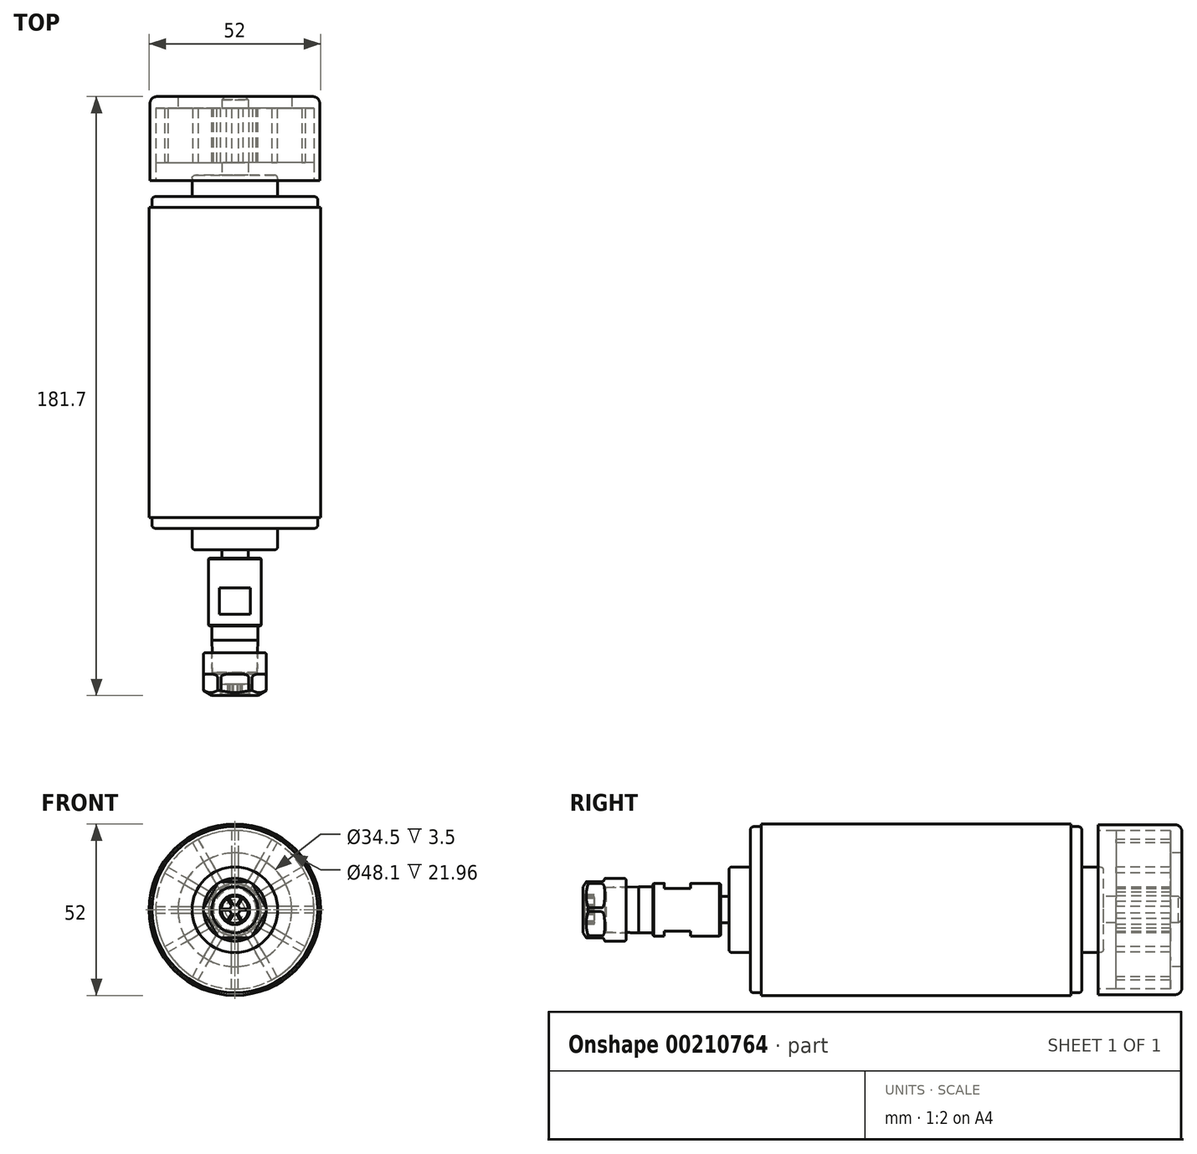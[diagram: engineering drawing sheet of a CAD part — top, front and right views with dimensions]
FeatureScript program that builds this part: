
annotation { "Feature Type Name" : "Feature", "Feature Type Description" : "" }
export const myFeature = defineFeature(function(context is Context, id is Id, definition is map)
    precondition{}
    {
        {
            var Q0;
            Q0=qCreatedBy(makeId("Right.planeOp"),FACE);
            var sketch = newSketch(context, id + "F0", { "sketchPlane" : qUnion([Q0])});
            skLineSegment(sketch, "E0", {"start": v(-129, 0) * mm, "end": v(123.78, 0) * mm, "construction": true});
            skLineSegment(sketch, "E1", {"start": v(-68.75, 0) * mm, "end": v(68.75, 0) * mm});
            skLineSegment(sketch, "E2", {"start": v(68.75, 0) * mm, "end": v(68.75, 25.75) * mm, "construction": true});
            skLineSegment(sketch, "E3", {"start": v(68.75, 25.75) * mm, "end": v(43.3, 25.75) * mm});
            skLineSegment(sketch, "E4", {"start": v(43.3, 25.75) * mm, "end": v(43.3, 24.05) * mm});
            skLineSegment(sketch, "E5", {"start": v(43.3, 24.05) * mm, "end": v(48.75, 24.05) * mm});
            skLineSegment(sketch, "E6", {"start": v(48.75, 24.05) * mm, "end": v(48.75, 4) * mm});
            skLineSegment(sketch, "E7", {"start": v(48.75, 4) * mm, "end": v(44.93, 4) * mm});
            skLineSegment(sketch, "E8", {"start": v(44.93, 4) * mm, "end": v(44.93, 13) * mm});
            skLineSegment(sketch, "E9", {"start": v(44.93, 13) * mm, "end": v(38.39, 13) * mm});
            skLineSegment(sketch, "E10", {"start": v(38.39, 13) * mm, "end": v(38.39, 25.2) * mm});
            skLineSegment(sketch, "E11", {"start": v(38.39, 25.2) * mm, "end": v(35.09, 25.2) * mm});
            skLineSegment(sketch, "E12", {"start": v(35.09, 25.2) * mm, "end": v(35.09, 26) * mm});
            skLineSegment(sketch, "E13", {"start": v(35.09, 26) * mm, "end": v(-58.91, 26) * mm});
            skLineSegment(sketch, "E14", {"start": v(-58.91, 26) * mm, "end": v(-58.91, 25.2) * mm});
            skLineSegment(sketch, "E15", {"start": v(-58.91, 25.2) * mm, "end": v(-62.21, 25.2) * mm});
            skLineSegment(sketch, "E16", {"start": v(-62.2, 25.2) * mm, "end": v(-62.2, 13) * mm});
            skLineSegment(sketch, "E17", {"start": v(-62.21, 13) * mm, "end": v(-68.75, 13) * mm});
            skLineSegment(sketch, "E18", {"start": v(-68.75, 13) * mm, "end": v(-68.75, 0) * mm});
            skLineSegment(sketch, "E19", {"start": v(68.75, 0) * mm, "end": v(68.75, 4) * mm});
            skLineSegment(sketch, "E20", {"start": v(68.75, 4) * mm, "end": v(65.25, 4) * mm});
            skLineSegment(sketch, "E21", {"start": v(65.25, 4) * mm, "end": v(65.25, 17.25) * mm});
            skLineSegment(sketch, "E22", {"start": v(65.25, 17.25) * mm, "end": v(68.75, 17.25) * mm});
            skLineSegment(sketch, "E23", {"start": v(68.75, 25.75) * mm, "end": v(68.75, 17.25) * mm});
            skLineSegment(sketch, "E24", {"start": v(-71.25, 4) * mm, "end": v(-68.75, 4) * mm});
            skLineSegment(sketch, "E25", {"start": v(-106.25, 0) * mm, "end": v(-106.25, 6.75) * mm});
            skLineSegment(sketch, "E26", {"start": v(-106.25, 6.75) * mm, "end": v(-96.15, 7) * mm});
            skLineSegment(sketch, "E27", {"start": v(-96.15, 7) * mm, "end": v(-91.85, 7) * mm});
            skLineSegment(sketch, "E28", {"start": v(-91.85, 7) * mm, "end": v(-91.85, 8) * mm});
            skLineSegment(sketch, "E29", {"start": v(-91.85, 8) * mm, "end": v(-71.25, 8) * mm});
            skLineSegment(sketch, "E30", {"start": v(-68.75, 0) * mm, "end": v(-106.25, 0) * mm});
            skLineSegment(sketch, "E31", {"start": v(-71.25, 8) * mm, "end": v(-71.25, 0) * mm});
            skSolve(sketch);
        }
        {
            var Q0;
            Q0=makeQuery(id+"F0.imprint","IMPRINT",FACE,{"disambiguationData":[TD([[makeQuery(id+"F0.imprint","IMPRINT",EDGE,{"derivedFrom":sQuery(id+"F0.wireOp",EDGE,"E1")}),1.0]])]});
            var Q1;
            {var subQ3=sQuery(id+"F0.wireOp",EDGE,"E24");Q1=makeQuery(id+"F0.imprint","IMPRINT",FACE,{"disambiguationData":[TD([[makeQuery(id+"F0.imprint","IMPRINT",EDGE,{"derivedFrom":subQ3}),-1.0]])]});}
            var Q2;
            {var subQ0=sQuery(id+"F0.wireOp",EDGE,"E25");Q2=makeQuery(id+"F0.imprint","IMPRINT",FACE,{"disambiguationData":[TD([[makeQuery(id+"F0.imprint","IMPRINT",EDGE,{"derivedFrom":subQ0}),-1.0]])]});}
            var Q3;
            Q3=sQuery(id+"F0.wireOp",EDGE,"E0");
            revolve(context, id + "F1", {"entities" : qUnion([Q0, Q1, Q2]), "axis" : qUnion([Q3]), "revolveType" : RevolveType.FULL});
        }
        {
            var Q0;
            Q0=makeQuery(id+"F1.opRevolve","SWEPT_EDGE",EDGE,{"disambiguationData":[OSD([sQuery(id+"F0.wireOp",EDGE,"E3"),sQuery(id+"F0.wireOp",EDGE,"E23")])]});
            fillet(context, id + "F2", {"entities" : qUnion([Q0]), "radius" : 2 * mm, "tangentPropagation" : true, "allowEdgeOverflow" : false});
        }
        {
            var Q0;
            Q0=makeQuery(id+"F1.opRevolve","SWEPT_EDGE",EDGE,{"disambiguationData":[OSD([sQuery(id+"F0.wireOp",EDGE,"E10"),sQuery(id+"F0.wireOp",EDGE,"E11")])]});
            var Q1;
            Q1=makeQuery(id+"F1.opRevolve","SWEPT_EDGE",EDGE,{"disambiguationData":[OSD([sQuery(id+"F0.wireOp",EDGE,"E15"),sQuery(id+"F0.wireOp",EDGE,"E16")])]});
            var Q2;
            Q2=makeQuery(id+"F1.opRevolve","SWEPT_EDGE",EDGE,{"disambiguationData":[OSD([sQuery(id+"F0.wireOp",EDGE,"E17"),sQuery(id+"F0.wireOp",EDGE,"E18")])]});
            var Q3;
            Q3=makeQuery(id+"F1.opRevolve","SWEPT_EDGE",EDGE,{"disambiguationData":[OSD([sQuery(id+"F0.wireOp",EDGE,"E8"),sQuery(id+"F0.wireOp",EDGE,"E9")])]});
            fillet(context, id + "F3", {"entities" : qUnion([Q0, Q1, Q2, Q3]), "radius" : 1 * mm, "tangentPropagation" : true, "allowEdgeOverflow" : false});
        }
        {
            var Q0;
            Q0=makeQuery(id+"F1.opRevolve","SWEPT_EDGE",EDGE,{"disambiguationData":[OSD([sQuery(id+"F0.wireOp",EDGE,"E19"),sQuery(id+"F0.wireOp",EDGE,"E20")])]});
            chamfer(context, id + "F4", {"entities" : qUnion([Q0]), "width" : 1 * mm, "tangentPropagation" : true});
        }
        {
            var Q0;
            Q0=makeQuery(id+"F1.opRevolve","SWEPT_EDGE",EDGE,{"disambiguationData":[OSD([sQuery(id+"F0.wireOp",EDGE,"E29"),sQuery(id+"F0.wireOp",EDGE,"E31")])]});
            var Q1;
            Q1=makeQuery(id+"F1.opRevolve","SWEPT_EDGE",EDGE,{"disambiguationData":[OSD([sQuery(id+"F0.wireOp",EDGE,"E28"),sQuery(id+"F0.wireOp",EDGE,"E29")])]});
            var Q2;
            Q2=makeQuery(id+"F1.opRevolve","SWEPT_EDGE",EDGE,{"disambiguationData":[OSD([sQuery(id+"F0.wireOp",EDGE,"E25"),sQuery(id+"F0.wireOp",EDGE,"E26")])]});
            chamfer(context, id + "F5", {"entities" : qUnion([Q0, Q1, Q2]), "width" : .3 * mm, "tangentPropagation" : true});
        }
        {
            var Q0;
            Q0=qCreatedBy(makeId("Right.planeOp"),FACE);
            var sketch = newSketch(context, id + "F6", { "sketchPlane" : qUnion([Q0])});
            skLineSegment(sketch, "E32.bottom", {"start": v(-88.35, 9) * mm, "end": v(-80.35, 9) * mm});
            skLineSegment(sketch, "E32.top", {"start": v(-88.35, 6.5) * mm, "end": v(-80.35, 6.5) * mm});
            skLineSegment(sketch, "E32.left", {"start": v(-88.35, 9) * mm, "end": v(-88.35, 6.5) * mm});
            skLineSegment(sketch, "E32.right", {"start": v(-80.35, 9) * mm, "end": v(-80.35, 6.5) * mm});
            skLineSegment(sketch, "E33", {"start": v(-60.08, 0) * mm, "end": v(-87.32, 0) * mm, "construction": true});
            skLineSegment(sketch, "E34.MirrorCS", {"start": v(-80.35, -9) * mm, "end": v(-80.35, -6.5) * mm});
            skLineSegment(sketch, "E35.MirrorCS", {"start": v(-88.35, -9) * mm, "end": v(-88.35, -6.5) * mm});
            skLineSegment(sketch, "E36.MirrorCS", {"start": v(-88.35, -9) * mm, "end": v(-80.35, -9) * mm});
            skLineSegment(sketch, "E37.MirrorCS", {"start": v(-88.35, -6.5) * mm, "end": v(-80.35, -6.5) * mm});
            skSolve(sketch);
        }
        {
            var Q0;
            Q0 = qSketchRegion(id + "F6", true);
            extrude(context, id + "F7", {"entities" : qUnion([Q0]), "operationType" : NewBodyOperationType.REMOVE, "endBound" : BoundingType.SYMMETRIC, "depth" : 25 * mm});
        }
        {
            var Q0;
            Q0=qCreatedBy(makeId("Right.planeOp"),FACE);
            var sketch = newSketch(context, id + "F8", { "sketchPlane" : qUnion([Q0])});
            skLineSegment(sketch, "E38", {"start": v(0, 0) * mm, "end": v(-99.95, 0) * mm, "construction": true});
            skLineSegment(sketch, "E39", {"start": v(-99.95, 0) * mm, "end": v(-112.95, 0) * mm});
            skLineSegment(sketch, "E40", {"start": v(-112.95, 0) * mm, "end": v(-112.95, 9.5) * mm});
            skLineSegment(sketch, "E41", {"start": v(-112.95, 9.5) * mm, "end": v(-99.95, 9.5) * mm});
            skLineSegment(sketch, "E42", {"start": v(-99.95, 9.5) * mm, "end": v(-99.95, 0) * mm});
            skLineSegment(sketch, "E43", {"start": v(-106.42, 0) * mm, "end": v(-106.42, 6.84) * mm});
            skLineSegment(sketch, "E44", {"start": v(-106.42, 6.84) * mm, "end": v(-99.95, 7.03) * mm});
            skSolve(sketch);
        }
        {
            var Q0;
            {var subQ3=sQuery(id+"F8.wireOp",EDGE,"E40");Q0=makeQuery(id+"F8.imprint","IMPRINT",FACE,{"disambiguationData":[TD([[makeQuery(id+"F8.imprint","IMPRINT",EDGE,{"derivedFrom":subQ3}),-1.0]])]});}
            var Q1;
            Q1=sQuery(id+"F8.wireOp",EDGE,"E38");
            revolve(context, id + "F9", {"entities" : qUnion([Q0]), "axis" : qUnion([Q1]), "revolveType" : RevolveType.FULL});
        }
        {
            var Q0;
            Q0=makeQuery(id+"F9.opRevolve","SWEPT_EDGE",EDGE,{"disambiguationData":[OSD([sQuery(id+"F8.wireOp",EDGE,"E41"),sQuery(id+"F8.wireOp",EDGE,"E42")])]});
            fillet(context, id + "F10", {"entities" : qUnion([Q0]), "radius" : .5 * mm, "tangentPropagation" : true, "allowEdgeOverflow" : false});
        }
        {
            var Q0;
            Q0=qCreatedBy(makeId("Right.planeOp"),FACE);
            var sketch = newSketch(context, id + "F11", { "sketchPlane" : qUnion([Q0])});
            skLineSegment(sketch, "E45", {"start": v(-112.95, 7) * mm, "end": v(-111.45, 9.5) * mm});
            skLineSegment(sketch, "E46", {"start": v(-111.45, 9.5) * mm, "end": v(-112.95, 9.5) * mm});
            skLineSegment(sketch, "E47", {"start": v(-112.95, 9.5) * mm, "end": v(-112.95, 7) * mm});
            skLineSegment(sketch, "E48", {"start": v(0, 0) * mm, "end": v(-3.44, 0) * mm});
            skLineSegment(sketch, "E49", {"start": v(-3.44, 0) * mm, "end": v(-117.43, 0) * mm, "construction": true});
            skSolve(sketch);
        }
        {
            var Q0;
            Q0 = qSketchRegion(id + "F11", true);
            var Q1;
            Q1=sQuery(id+"F11.wireOp",EDGE,"E49");
            revolve(context, id + "F12", {"operationType" : NewBodyOperationType.REMOVE, "entities" : qUnion([Q0]), "axis" : qUnion([Q1]), "revolveType" : RevolveType.FULL, "oppositeDirection" : true});
        }
        {
            var Q0;
            Q0=makeQuery(id+"F9.opRevolve","SWEPT_FACE",FACE,{"disambiguationData":[OSD([sQuery(id+"F8.wireOp",EDGE,"E40")])]});
            var sketch = newSketch(context, id + "F13", { "sketchPlane" : qUnion([Q0])});
            skCircle(sketch, "E50.cCircle", {"center": v(0, 0) * mm, "radius": 8.5 * mm, "construction": true});
            skLineSegment(sketch, "E50.0", {"start": v(-4.9, 8.5) * mm, "end": v(4.9, 8.5) * mm});
            skLineSegment(sketch, "E50.1", {"start": v(4.9, 8.5) * mm, "end": v(9.81, 0) * mm});
            skLineSegment(sketch, "E50.2", {"start": v(9.81, 0) * mm, "end": v(4.9, -8.5) * mm});
            skLineSegment(sketch, "E50.3", {"start": v(4.9, -8.5) * mm, "end": v(-4.9, -8.5) * mm});
            skLineSegment(sketch, "E50.4", {"start": v(-4.9, -8.5) * mm, "end": v(-9.81, 0) * mm});
            skLineSegment(sketch, "E50.5", {"start": v(-9.81, 0) * mm, "end": v(-4.9, 8.5) * mm});
            skPoint(sketch, "E50.0.midPoint", {"position": v(0, 8.5) * mm});
            skCircle(sketch, "E51", {"center": v(0, 0) * mm, "radius": 12 * mm});
            skLineSegment(sketch, "E52", {"start": v(0, 8.5) * mm, "end": v(0, 9.5) * mm, "construction": true});
            skSolve(sketch);
        }
        {
            var Q0;
            Q0=makeQuery(id+"F13.imprint","IMPRINT",FACE,{"disambiguationData":[TD([[makeQuery(id+"F13.imprint","IMPRINT",EDGE,{"derivedFrom":sQuery(id+"F13.wireOp",EDGE,"E50.0")}),1.0]])]});
            extrude(context, id + "F14", {"entities" : qUnion([Q0]), "operationType" : NewBodyOperationType.REMOVE, "oppositeDirection" : true, "depth" : 6.5 * mm});
        }
        {
            var Q0;
            Q0=makeQuery(id+"F14.boolean.opBoolean","COPY",EDGE,{"derivedFrom":makeQuery(id+"F14.opExtrude","CAP_EDGE",EDGE,{"disambiguationData":[OSD([sQuery(id+"F13.wireOp",EDGE,"E50.0")])],"isStart":false})});
            var Q1;
            Q1=makeQuery(id+"F14.boolean.opBoolean","COPY",EDGE,{"derivedFrom":makeQuery(id+"F14.opExtrude","CAP_EDGE",EDGE,{"disambiguationData":[OSD([sQuery(id+"F13.wireOp",EDGE,"E50.1")])],"isStart":false})});
            var Q2;
            Q2=makeQuery(id+"F14.boolean.opBoolean","COPY",EDGE,{"derivedFrom":makeQuery(id+"F14.opExtrude","CAP_EDGE",EDGE,{"disambiguationData":[OSD([sQuery(id+"F13.wireOp",EDGE,"E50.2")])],"isStart":false})});
            var Q3;
            Q3=makeQuery(id+"F14.boolean.opBoolean","COPY",EDGE,{"derivedFrom":makeQuery(id+"F14.opExtrude","CAP_EDGE",EDGE,{"disambiguationData":[OSD([sQuery(id+"F13.wireOp",EDGE,"E50.3")])],"isStart":false})});
            var Q4;
            Q4=makeQuery(id+"F14.boolean.opBoolean","COPY",EDGE,{"derivedFrom":makeQuery(id+"F14.opExtrude","CAP_EDGE",EDGE,{"disambiguationData":[OSD([sQuery(id+"F13.wireOp",EDGE,"E50.4")])],"isStart":false})});
            var Q5;
            Q5=makeQuery(id+"F14.boolean.opBoolean","COPY",EDGE,{"derivedFrom":makeQuery(id+"F14.opExtrude","CAP_EDGE",EDGE,{"disambiguationData":[OSD([sQuery(id+"F13.wireOp",EDGE,"E50.5")])],"isStart":false})});
            fillet(context, id + "F15", {"entities" : qUnion([Q0, Q1, Q2, Q3, Q4, Q5]), "radius" : 1 * mm, "tangentPropagation" : true, "allowEdgeOverflow" : false});
        }
        {
            var Q0;
            Q0=makeQuery(id+"F9.opRevolve","SWEPT_FACE",FACE,{"disambiguationData":[OSD([sQuery(id+"F8.wireOp",EDGE,"E40")])]});
            var sketch = newSketch(context, id + "F16", { "sketchPlane" : qUnion([Q0])});
            skCircle(sketch, "E53", {"center": v(0, 0) * mm, "radius": 4.5 * mm});
            skSolve(sketch);
        }
        {
            var Q0;
            Q0 = qSketchRegion(id + "F16", true);
            extrude(context, id + "F17", {"entities" : qUnion([Q0]), "operationType" : NewBodyOperationType.REMOVE, "oppositeDirection" : true, "depth" : .4 * mm});
        }
        {
            var Q0;
            Q0=makeQuery(id+"F17.boolean.opBoolean","COPY",FACE,{"derivedFrom":makeQuery(id+"F17.opExtrude","CAP_FACE",FACE,{"disambiguationData":[OSD([sQuery(id+"F16.wireOp",EDGE,"E53")])],"isStart":false})});
            var sketch = newSketch(context, id + "F18", { "sketchPlane" : qUnion([Q0])});
            skCircle(sketch, "E54", {"center": v(0, 0) * mm, "radius": 4.5 * mm});
            skArc(sketch, "E55", {"start": v(-0.92, 1.19) * mm, "mid": v(-1.3, 0.75) * mm, "end": v(-1.49, 0.2) * mm});
            skLineSegment(sketch, "E56", {"start": v(0, 4.5) * mm, "end": v(0, 0) * mm, "construction": true});
            skLineSegment(sketch, "E57", {"start": v(-2.25, 3.9) * mm, "end": v(0, 0) * mm, "construction": true});
            skLineSegment(sketch, "E58", {"start": v(-2.22, 3.45) * mm, "end": v(-0.92, 1.19) * mm});
            skLineSegment(sketch, "E59", {"start": v(-1.87, 3.65) * mm, "end": v(-0.57, 1.39) * mm});
            skArc(sketch, "E60", {"start": v(-2.22, 3.45) * mm, "mid": v(-3.55, 2.05) * mm, "end": v(-4.1, 0.2) * mm});
            skLineSegment(sketch, "E61.1.0", {"start": v(-4.1, 0.2) * mm, "end": v(-1.49, 0.2) * mm});
            skLineSegment(sketch, "E61.1.1", {"start": v(-4.1, -0.2) * mm, "end": v(-1.49, -0.2) * mm});
            skLineSegment(sketch, "E61.2.0", {"start": v(-2.22, -3.45) * mm, "end": v(-0.92, -1.19) * mm});
            skLineSegment(sketch, "E61.2.1", {"start": v(-1.87, -3.65) * mm, "end": v(-0.57, -1.39) * mm});
            skLineSegment(sketch, "E61.3.0", {"start": v(1.87, -3.65) * mm, "end": v(0.57, -1.39) * mm});
            skLineSegment(sketch, "E61.3.1", {"start": v(2.22, -3.45) * mm, "end": v(0.92, -1.19) * mm});
            skLineSegment(sketch, "E61.4.0", {"start": v(4.1, -0.2) * mm, "end": v(1.49, -0.2) * mm});
            skLineSegment(sketch, "E61.4.1", {"start": v(4.1, 0.2) * mm, "end": v(1.49, 0.2) * mm});
            skLineSegment(sketch, "E61.5.0", {"start": v(2.22, 3.45) * mm, "end": v(0.92, 1.19) * mm});
            skLineSegment(sketch, "E61.5.1", {"start": v(1.87, 3.65) * mm, "end": v(0.57, 1.39) * mm});
            skArc(sketch, "E62.trimOffspring", {"start": v(0.57, 1.39) * mm, "mid": v(0, 1.5) * mm, "end": v(-0.57, 1.39) * mm});
            skArc(sketch, "E63.trimOffspring", {"start": v(1.87, 3.65) * mm, "mid": v(0, 4.1) * mm, "end": v(-1.87, 3.65) * mm});
            skArc(sketch, "E64.trimOffspring", {"start": v(4.1, 0.2) * mm, "mid": v(3.55, 2.05) * mm, "end": v(2.22, 3.45) * mm});
            skArc(sketch, "E65.trimOffspring", {"start": v(1.49, 0.2) * mm, "mid": v(1.3, 0.75) * mm, "end": v(0.92, 1.19) * mm});
            skArc(sketch, "E66.trimOffspring", {"start": v(0.92, -1.19) * mm, "mid": v(1.3, -0.75) * mm, "end": v(1.49, -0.2) * mm});
            skArc(sketch, "E67.trimOffspring", {"start": v(2.22, -3.45) * mm, "mid": v(3.55, -2.05) * mm, "end": v(4.1, -0.2) * mm});
            skArc(sketch, "E68.trimOffspring", {"start": v(-1.87, -3.65) * mm, "mid": v(0, -4.1) * mm, "end": v(1.87, -3.65) * mm});
            skArc(sketch, "E69.trimOffspring", {"start": v(-0.57, -1.39) * mm, "mid": v(0, -1.5) * mm, "end": v(0.57, -1.39) * mm});
            skArc(sketch, "E70.trimOffspring", {"start": v(-1.49, -0.2) * mm, "mid": v(-1.3, -0.75) * mm, "end": v(-0.92, -1.19) * mm});
            skArc(sketch, "E71.trimOffspring", {"start": v(-4.1, -0.2) * mm, "mid": v(-3.55, -2.05) * mm, "end": v(-2.22, -3.45) * mm});
            skSolve(sketch);
        }
        {
            var Q0;
            Q0=makeQuery(id+"F18.imprint","IMPRINT",FACE,{"disambiguationData":[TD([[makeQuery(id+"F18.imprint","IMPRINT",EDGE,{"derivedFrom":sQuery(id+"F18.wireOp",EDGE,"E54")}),1.0]])]});
            extrude(context, id + "F19", {"entities" : qUnion([Q0]), "operationType" : NewBodyOperationType.REMOVE, "oppositeDirection" : true, "depth" : 3 * mm});
        }
        {
            var Q0;
            Q0=makeQuery(id+"F1.opRevolve","SWEPT_FACE",FACE,{"disambiguationData":[OSD([sQuery(id+"F0.wireOp",EDGE,"E21")])]});
            var sketch = newSketch(context, id + "F20", { "sketchPlane" : qUnion([Q0])});
            skArc(sketch, "E72", {"start": v(-4.33, 5.5) * mm, "mid": v(-4.95, 4.95) * mm, "end": v(-5.5, 4.33) * mm});
            skArc(sketch, "E73", {"start": v(-1, 17.22) * mm, "mid": v(-4.46, 16.66) * mm, "end": v(-7.74, 15.41) * mm});
            skLineSegment(sketch, "E74", {"start": v(0, 0) * mm, "end": v(0, 17.25) * mm, "construction": true});
            skLineSegment(sketch, "E75", {"start": v(0, 0) * mm, "end": v(4.46, 16.66) * mm, "construction": true});
            skLineSegment(sketch, "E76", {"start": v(-1, 17.22) * mm, "end": v(-1, 6.93) * mm});
            skLineSegment(sketch, "E77", {"start": v(1, 17.22) * mm, "end": v(1, 6.93) * mm});
            skLineSegment(sketch, "E78.1.0", {"start": v(-7.74, 15.41) * mm, "end": v(-2.6, 6.5) * mm});
            skLineSegment(sketch, "E78.1.1", {"start": v(-9.48, 14.41) * mm, "end": v(-4.33, 5.5) * mm});
            skLineSegment(sketch, "E78.2.0", {"start": v(-14.41, 9.48) * mm, "end": v(-5.5, 4.33) * mm});
            skLineSegment(sketch, "E78.2.1", {"start": v(-15.41, 7.74) * mm, "end": v(-6.5, 2.6) * mm});
            skLineSegment(sketch, "E78.3.0", {"start": v(-17.22, 1) * mm, "end": v(-6.93, 1) * mm});
            skLineSegment(sketch, "E78.3.1", {"start": v(-17.22, -1) * mm, "end": v(-6.93, -1) * mm});
            skLineSegment(sketch, "E78.4.0", {"start": v(-15.41, -7.74) * mm, "end": v(-6.5, -2.6) * mm});
            skLineSegment(sketch, "E78.4.1", {"start": v(-14.41, -9.48) * mm, "end": v(-5.5, -4.33) * mm});
            skLineSegment(sketch, "E78.5.0", {"start": v(-9.48, -14.41) * mm, "end": v(-4.33, -5.5) * mm});
            skLineSegment(sketch, "E78.5.1", {"start": v(-7.74, -15.41) * mm, "end": v(-2.6, -6.5) * mm});
            skLineSegment(sketch, "E78.6.0", {"start": v(-1, -17.22) * mm, "end": v(-1, -6.93) * mm});
            skLineSegment(sketch, "E78.6.1", {"start": v(1, -17.22) * mm, "end": v(1, -6.93) * mm});
            skLineSegment(sketch, "E78.7.0", {"start": v(7.74, -15.41) * mm, "end": v(2.6, -6.5) * mm});
            skLineSegment(sketch, "E78.7.1", {"start": v(9.48, -14.41) * mm, "end": v(4.33, -5.5) * mm});
            skLineSegment(sketch, "E78.8.0", {"start": v(14.41, -9.48) * mm, "end": v(5.5, -4.33) * mm});
            skLineSegment(sketch, "E78.8.1", {"start": v(15.41, -7.74) * mm, "end": v(6.5, -2.6) * mm});
            skLineSegment(sketch, "E78.9.0", {"start": v(17.22, -1) * mm, "end": v(6.93, -1) * mm});
            skLineSegment(sketch, "E78.9.1", {"start": v(17.22, 1) * mm, "end": v(6.93, 1) * mm});
            skLineSegment(sketch, "E78.10.0", {"start": v(15.41, 7.74) * mm, "end": v(6.5, 2.6) * mm});
            skLineSegment(sketch, "E78.10.1", {"start": v(14.41, 9.48) * mm, "end": v(5.5, 4.33) * mm});
            skLineSegment(sketch, "E78.11.0", {"start": v(9.48, 14.41) * mm, "end": v(4.33, 5.5) * mm});
            skLineSegment(sketch, "E78.11.1", {"start": v(7.74, 15.41) * mm, "end": v(2.6, 6.5) * mm});
            skArc(sketch, "E79.trimOffspring", {"start": v(7.74, 15.41) * mm, "mid": v(4.46, 16.66) * mm, "end": v(1, 17.22) * mm});
            skArc(sketch, "E80.trimOffspring", {"start": v(14.41, 9.48) * mm, "mid": v(12.2, 12.2) * mm, "end": v(9.48, 14.41) * mm});
            skArc(sketch, "E81.trimOffspring", {"start": v(17.22, 1) * mm, "mid": v(16.66, 4.46) * mm, "end": v(15.41, 7.74) * mm});
            skArc(sketch, "E82.trimOffspring", {"start": v(15.41, -7.74) * mm, "mid": v(16.66, -4.46) * mm, "end": v(17.22, -1) * mm});
            skArc(sketch, "E83.trimOffspring", {"start": v(9.48, -14.41) * mm, "mid": v(12.2, -12.2) * mm, "end": v(14.41, -9.48) * mm});
            skArc(sketch, "E84.trimOffspring", {"start": v(1, -17.22) * mm, "mid": v(4.46, -16.66) * mm, "end": v(7.74, -15.41) * mm});
            skArc(sketch, "E85.trimOffspring", {"start": v(-7.74, -15.41) * mm, "mid": v(-4.46, -16.66) * mm, "end": v(-1, -17.22) * mm});
            skArc(sketch, "E86.trimOffspring", {"start": v(-14.41, -9.48) * mm, "mid": v(-12.2, -12.2) * mm, "end": v(-9.48, -14.41) * mm});
            skArc(sketch, "E87.trimOffspring", {"start": v(-17.22, -1) * mm, "mid": v(-16.66, -4.46) * mm, "end": v(-15.41, -7.74) * mm});
            skArc(sketch, "E88.trimOffspring", {"start": v(-15.41, 7.74) * mm, "mid": v(-16.66, 4.46) * mm, "end": v(-17.22, 1) * mm});
            skArc(sketch, "E89.trimOffspring", {"start": v(-9.48, 14.41) * mm, "mid": v(-12.2, 12.2) * mm, "end": v(-14.41, 9.48) * mm});
            skArc(sketch, "E90.trimOffspring", {"start": v(-1, 6.93) * mm, "mid": v(-1.81, 6.76) * mm, "end": v(-2.6, 6.5) * mm});
            skArc(sketch, "E91.trimOffspring", {"start": v(2.6, 6.5) * mm, "mid": v(1.81, 6.76) * mm, "end": v(1, 6.93) * mm});
            skArc(sketch, "E92.trimOffspring", {"start": v(6.93, 1) * mm, "mid": v(6.76, 1.81) * mm, "end": v(6.5, 2.6) * mm});
            skArc(sketch, "E93.trimOffspring", {"start": v(6.5, -2.6) * mm, "mid": v(6.76, -1.81) * mm, "end": v(6.93, -1) * mm});
            skArc(sketch, "E94.trimOffspring", {"start": v(4.33, -5.5) * mm, "mid": v(4.95, -4.95) * mm, "end": v(5.5, -4.33) * mm});
            skArc(sketch, "E95.trimOffspring", {"start": v(-6.5, 2.6) * mm, "mid": v(-6.76, 1.81) * mm, "end": v(-6.93, 1) * mm});
            skArc(sketch, "E96.trimOffspring", {"start": v(-6.93, -1) * mm, "mid": v(-6.76, -1.81) * mm, "end": v(-6.5, -2.6) * mm});
            skArc(sketch, "E97.trimOffspring", {"start": v(-2.6, -6.5) * mm, "mid": v(-1.81, -6.76) * mm, "end": v(-1, -6.93) * mm});
            skArc(sketch, "E98.trimOffspring", {"start": v(1, -6.93) * mm, "mid": v(1.81, -6.76) * mm, "end": v(2.6, -6.5) * mm});
            skArc(sketch, "E99", {"start": v(-5.5, -4.33) * mm, "mid": v(-4.95, -4.95) * mm, "end": v(-4.33, -5.5) * mm});
            skArc(sketch, "E100", {"start": v(5.5, 4.33) * mm, "mid": v(4.95, 4.95) * mm, "end": v(4.33, 5.5) * mm});
            skSolve(sketch);
        }
        {
            var Q0;
            Q0 = qSketchRegion(id + "F20", true);
            extrude(context, id + "F21", {"entities" : qUnion([Q0]), "operationType" : NewBodyOperationType.REMOVE, "oppositeDirection" : true, "depth" : 20 * mm});
        }
        {
            var Q0;
            Q0=makeQuery(id+"F1.opRevolve","SWEPT_FACE",FACE,{"disambiguationData":[OSD([sQuery(id+"F0.wireOp",EDGE,"E6")])]});
            var sketch = newSketch(context, id + "F22", { "sketchPlane" : qUnion([Q0])});
            skCircle(sketch, "E101", {"center": v(0, 0) * mm, "radius": 24.05 * mm});
            skArc(sketch, "E102.0", {"start": v(1, 6.93) * mm, "mid": v(1.81, 6.76) * mm, "end": v(2.6, 6.5) * mm});
            skArc(sketch, "E102.1", {"start": v(4.33, 5.5) * mm, "mid": v(4.95, 4.95) * mm, "end": v(5.5, 4.33) * mm});
            skArc(sketch, "E102.2", {"start": v(6.5, 2.6) * mm, "mid": v(6.76, 1.81) * mm, "end": v(6.93, 1) * mm});
            skArc(sketch, "E102.3", {"start": v(6.93, -1) * mm, "mid": v(6.76, -1.81) * mm, "end": v(6.5, -2.6) * mm});
            skArc(sketch, "E102.4", {"start": v(5.5, -4.33) * mm, "mid": v(4.95, -4.95) * mm, "end": v(4.33, -5.5) * mm});
            skArc(sketch, "E102.5", {"start": v(2.6, -6.5) * mm, "mid": v(1.81, -6.76) * mm, "end": v(1, -6.93) * mm});
            skLineSegment(sketch, "E102.6", {"start": v(1, -24.03) * mm, "end": v(1, -6.93) * mm});
            skLineSegment(sketch, "E102.7", {"start": v(11.15, -21.3) * mm, "end": v(2.6, -6.5) * mm});
            skLineSegment(sketch, "E102.8", {"start": v(12.88, -20.3) * mm, "end": v(4.33, -5.5) * mm});
            skLineSegment(sketch, "E102.9", {"start": v(20.3, -12.88) * mm, "end": v(5.5, -4.33) * mm});
            skLineSegment(sketch, "E102.10", {"start": v(21.3, -11.15) * mm, "end": v(6.5, -2.6) * mm});
            skLineSegment(sketch, "E102.11", {"start": v(24.03, -1) * mm, "end": v(6.93, -1) * mm});
            skLineSegment(sketch, "E102.12", {"start": v(24.03, 1) * mm, "end": v(6.93, 1) * mm});
            skLineSegment(sketch, "E102.13", {"start": v(21.3, 11.15) * mm, "end": v(6.5, 2.6) * mm});
            skLineSegment(sketch, "E102.14", {"start": v(20.3, 12.88) * mm, "end": v(5.5, 4.33) * mm});
            skLineSegment(sketch, "E102.15", {"start": v(12.88, 20.3) * mm, "end": v(4.33, 5.5) * mm});
            skLineSegment(sketch, "E102.16", {"start": v(11.15, 21.3) * mm, "end": v(2.6, 6.5) * mm});
            skLineSegment(sketch, "E102.17", {"start": v(1, 24.03) * mm, "end": v(1, 6.93) * mm});
            skLineSegment(sketch, "E102.18", {"start": v(-1, 24.03) * mm, "end": v(-1, 6.93) * mm});
            skArc(sketch, "E102.19", {"start": v(-2.6, 6.5) * mm, "mid": v(-1.81, 6.76) * mm, "end": v(-1, 6.93) * mm});
            skLineSegment(sketch, "E102.20", {"start": v(-11.15, 21.3) * mm, "end": v(-2.6, 6.5) * mm});
            skLineSegment(sketch, "E102.21", {"start": v(-12.88, 20.3) * mm, "end": v(-4.33, 5.5) * mm});
            skArc(sketch, "E102.22", {"start": v(-5.5, 4.33) * mm, "mid": v(-4.95, 4.95) * mm, "end": v(-4.33, 5.5) * mm});
            skLineSegment(sketch, "E102.23", {"start": v(-20.3, 12.88) * mm, "end": v(-5.5, 4.33) * mm});
            skLineSegment(sketch, "E102.24", {"start": v(-21.3, 11.15) * mm, "end": v(-6.5, 2.6) * mm});
            skArc(sketch, "E102.25", {"start": v(-6.93, 1) * mm, "mid": v(-6.76, 1.81) * mm, "end": v(-6.5, 2.6) * mm});
            skLineSegment(sketch, "E102.26", {"start": v(-24.03, 1) * mm, "end": v(-6.93, 1) * mm});
            skLineSegment(sketch, "E102.27", {"start": v(-24.03, -1) * mm, "end": v(-6.93, -1) * mm});
            skArc(sketch, "E102.28", {"start": v(-6.5, -2.6) * mm, "mid": v(-6.76, -1.81) * mm, "end": v(-6.93, -1) * mm});
            skLineSegment(sketch, "E102.29", {"start": v(-21.3, -11.15) * mm, "end": v(-6.5, -2.6) * mm});
            skLineSegment(sketch, "E102.30", {"start": v(-20.3, -12.88) * mm, "end": v(-5.5, -4.33) * mm});
            skArc(sketch, "E102.31", {"start": v(-4.33, -5.5) * mm, "mid": v(-4.95, -4.95) * mm, "end": v(-5.5, -4.33) * mm});
            skLineSegment(sketch, "E102.32", {"start": v(-12.88, -20.3) * mm, "end": v(-4.33, -5.5) * mm});
            skLineSegment(sketch, "E102.33", {"start": v(-11.15, -21.3) * mm, "end": v(-2.6, -6.5) * mm});
            skArc(sketch, "E102.34", {"start": v(-1, -6.93) * mm, "mid": v(-1.81, -6.76) * mm, "end": v(-2.6, -6.5) * mm});
            skLineSegment(sketch, "E102.35", {"start": v(-1, -24.03) * mm, "end": v(-1, -6.93) * mm});
            skPoint(sketch, "E103.orphan", {"position": v(-7.74, 15.41) * mm});
            skPoint(sketch, "E104.orphan", {"position": v(-1, 17.22) * mm});
            skPoint(sketch, "E105.orphan", {"position": v(1, 17.22) * mm});
            skPoint(sketch, "E106.orphan", {"position": v(7.74, 15.41) * mm});
            skPoint(sketch, "E107.orphan", {"position": v(9.48, 14.41) * mm});
            skPoint(sketch, "E108.orphan", {"position": v(14.41, 9.48) * mm});
            skPoint(sketch, "E109.orphan", {"position": v(15.41, 7.74) * mm});
            skPoint(sketch, "E110.orphan", {"position": v(17.22, 1) * mm});
            skPoint(sketch, "E111.orphan", {"position": v(17.22, -1) * mm});
            skPoint(sketch, "E112.orphan", {"position": v(15.41, -7.74) * mm});
            skPoint(sketch, "E113.orphan", {"position": v(14.41, -9.48) * mm});
            skPoint(sketch, "E114.orphan", {"position": v(9.48, -14.41) * mm});
            skPoint(sketch, "E115.orphan", {"position": v(7.74, -15.41) * mm});
            skPoint(sketch, "E116.orphan", {"position": v(1, -17.22) * mm});
            skPoint(sketch, "E117.orphan", {"position": v(-1, -17.22) * mm});
            skPoint(sketch, "E118.orphan", {"position": v(-7.74, -15.41) * mm});
            skPoint(sketch, "E119.orphan", {"position": v(-9.48, -14.41) * mm});
            skPoint(sketch, "E120.orphan", {"position": v(-14.41, -9.48) * mm});
            skPoint(sketch, "E121.orphan", {"position": v(-15.41, -7.74) * mm});
            skPoint(sketch, "E122.orphan", {"position": v(-17.22, -1) * mm});
            skPoint(sketch, "E123.orphan", {"position": v(-17.22, 1) * mm});
            skPoint(sketch, "E124.orphan", {"position": v(-15.41, 7.74) * mm});
            skPoint(sketch, "E125.orphan", {"position": v(-14.41, 9.48) * mm});
            skPoint(sketch, "E126.orphan", {"position": v(-9.48, 14.41) * mm});
            skSolve(sketch);
        }
        {
            var Q0;
            {var subQ5=makeQuery(id+"F21.boolean.opBoolean","INTERSECT",EDGE,{"derivedFrom":[makeQuery(id+"F1.opRevolve","SWEPT_FACE",FACE,{"disambiguationData":[OSD([sQuery(id+"F0.wireOp",EDGE,"E6")])]}),makeQuery(id+"F21.opExtrude","SWEPT_FACE",FACE,{"disambiguationData":[OSD([sQuery(id+"F20.wireOp",EDGE,"E81.trimOffspring")])]})]});Q0=makeQuery(id+"F22.imprint","IMPRINT",FACE,{"disambiguationData":[TD([[makeQuery(id+"F22.imprint","IMPRINT",EDGE,{"derivedFrom":subQ5}),-1.0]])]});}
            var Q1;
            {var subQ5=makeQuery(id+"F21.boolean.opBoolean","INTERSECT",EDGE,{"derivedFrom":[makeQuery(id+"F1.opRevolve","SWEPT_FACE",FACE,{"disambiguationData":[OSD([sQuery(id+"F0.wireOp",EDGE,"E6")])]}),makeQuery(id+"F21.opExtrude","SWEPT_FACE",FACE,{"disambiguationData":[OSD([sQuery(id+"F20.wireOp",EDGE,"E80.trimOffspring")])]})]});Q1=makeQuery(id+"F22.imprint","IMPRINT",FACE,{"disambiguationData":[TD([[makeQuery(id+"F22.imprint","IMPRINT",EDGE,{"derivedFrom":subQ5}),-1.0]])]});}
            var Q2;
            {var subQ5=makeQuery(id+"F21.boolean.opBoolean","INTERSECT",EDGE,{"derivedFrom":[makeQuery(id+"F1.opRevolve","SWEPT_FACE",FACE,{"disambiguationData":[OSD([sQuery(id+"F0.wireOp",EDGE,"E6")])]}),makeQuery(id+"F21.opExtrude","SWEPT_FACE",FACE,{"disambiguationData":[OSD([sQuery(id+"F20.wireOp",EDGE,"E79.trimOffspring")])]})]});Q2=makeQuery(id+"F22.imprint","IMPRINT",FACE,{"disambiguationData":[TD([[makeQuery(id+"F22.imprint","IMPRINT",EDGE,{"derivedFrom":subQ5}),-1.0]])]});}
            var Q3;
            {var subQ5=makeQuery(id+"F21.boolean.opBoolean","INTERSECT",EDGE,{"derivedFrom":[makeQuery(id+"F1.opRevolve","SWEPT_FACE",FACE,{"disambiguationData":[OSD([sQuery(id+"F0.wireOp",EDGE,"E6")])]}),makeQuery(id+"F21.opExtrude","SWEPT_FACE",FACE,{"disambiguationData":[OSD([sQuery(id+"F20.wireOp",EDGE,"E82.trimOffspring")])]})]});Q3=makeQuery(id+"F22.imprint","IMPRINT",FACE,{"disambiguationData":[TD([[makeQuery(id+"F22.imprint","IMPRINT",EDGE,{"derivedFrom":subQ5}),-1.0]])]});}
            var Q4;
            {var subQ5=makeQuery(id+"F21.boolean.opBoolean","INTERSECT",EDGE,{"derivedFrom":[makeQuery(id+"F1.opRevolve","SWEPT_FACE",FACE,{"disambiguationData":[OSD([sQuery(id+"F0.wireOp",EDGE,"E6")])]}),makeQuery(id+"F21.opExtrude","SWEPT_FACE",FACE,{"disambiguationData":[OSD([sQuery(id+"F20.wireOp",EDGE,"E83.trimOffspring")])]})]});Q4=makeQuery(id+"F22.imprint","IMPRINT",FACE,{"disambiguationData":[TD([[makeQuery(id+"F22.imprint","IMPRINT",EDGE,{"derivedFrom":subQ5}),-1.0]])]});}
            var Q5;
            {var subQ5=makeQuery(id+"F21.boolean.opBoolean","INTERSECT",EDGE,{"derivedFrom":[makeQuery(id+"F1.opRevolve","SWEPT_FACE",FACE,{"disambiguationData":[OSD([sQuery(id+"F0.wireOp",EDGE,"E6")])]}),makeQuery(id+"F21.opExtrude","SWEPT_FACE",FACE,{"disambiguationData":[OSD([sQuery(id+"F20.wireOp",EDGE,"E84.trimOffspring")])]})]});Q5=makeQuery(id+"F22.imprint","IMPRINT",FACE,{"disambiguationData":[TD([[makeQuery(id+"F22.imprint","IMPRINT",EDGE,{"derivedFrom":subQ5}),-1.0]])]});}
            var Q6;
            {var subQ5=makeQuery(id+"F21.boolean.opBoolean","INTERSECT",EDGE,{"derivedFrom":[makeQuery(id+"F1.opRevolve","SWEPT_FACE",FACE,{"disambiguationData":[OSD([sQuery(id+"F0.wireOp",EDGE,"E6")])]}),makeQuery(id+"F21.opExtrude","SWEPT_FACE",FACE,{"disambiguationData":[OSD([sQuery(id+"F20.wireOp",EDGE,"E86.trimOffspring")])]})]});Q6=makeQuery(id+"F22.imprint","IMPRINT",FACE,{"disambiguationData":[TD([[makeQuery(id+"F22.imprint","IMPRINT",EDGE,{"derivedFrom":subQ5}),-1.0]])]});}
            var Q7;
            {var subQ5=makeQuery(id+"F21.boolean.opBoolean","INTERSECT",EDGE,{"derivedFrom":[makeQuery(id+"F1.opRevolve","SWEPT_FACE",FACE,{"disambiguationData":[OSD([sQuery(id+"F0.wireOp",EDGE,"E6")])]}),makeQuery(id+"F21.opExtrude","SWEPT_FACE",FACE,{"disambiguationData":[OSD([sQuery(id+"F20.wireOp",EDGE,"E85.trimOffspring")])]})]});Q7=makeQuery(id+"F22.imprint","IMPRINT",FACE,{"disambiguationData":[TD([[makeQuery(id+"F22.imprint","IMPRINT",EDGE,{"derivedFrom":subQ5}),-1.0]])]});}
            var Q8;
            {var subQ5=makeQuery(id+"F21.boolean.opBoolean","INTERSECT",EDGE,{"derivedFrom":[makeQuery(id+"F1.opRevolve","SWEPT_FACE",FACE,{"disambiguationData":[OSD([sQuery(id+"F0.wireOp",EDGE,"E6")])]}),makeQuery(id+"F21.opExtrude","SWEPT_FACE",FACE,{"disambiguationData":[OSD([sQuery(id+"F20.wireOp",EDGE,"E87.trimOffspring")])]})]});Q8=makeQuery(id+"F22.imprint","IMPRINT",FACE,{"disambiguationData":[TD([[makeQuery(id+"F22.imprint","IMPRINT",EDGE,{"derivedFrom":subQ5}),-1.0]])]});}
            var Q9;
            {var subQ5=makeQuery(id+"F21.boolean.opBoolean","INTERSECT",EDGE,{"derivedFrom":[makeQuery(id+"F1.opRevolve","SWEPT_FACE",FACE,{"disambiguationData":[OSD([sQuery(id+"F0.wireOp",EDGE,"E6")])]}),makeQuery(id+"F21.opExtrude","SWEPT_FACE",FACE,{"disambiguationData":[OSD([sQuery(id+"F20.wireOp",EDGE,"E88.trimOffspring")])]})]});Q9=makeQuery(id+"F22.imprint","IMPRINT",FACE,{"disambiguationData":[TD([[makeQuery(id+"F22.imprint","IMPRINT",EDGE,{"derivedFrom":subQ5}),-1.0]])]});}
            var Q10;
            {var subQ5=makeQuery(id+"F21.boolean.opBoolean","INTERSECT",EDGE,{"derivedFrom":[makeQuery(id+"F1.opRevolve","SWEPT_FACE",FACE,{"disambiguationData":[OSD([sQuery(id+"F0.wireOp",EDGE,"E6")])]}),makeQuery(id+"F21.opExtrude","SWEPT_FACE",FACE,{"disambiguationData":[OSD([sQuery(id+"F20.wireOp",EDGE,"E89.trimOffspring")])]})]});Q10=makeQuery(id+"F22.imprint","IMPRINT",FACE,{"disambiguationData":[TD([[makeQuery(id+"F22.imprint","IMPRINT",EDGE,{"derivedFrom":subQ5}),-1.0]])]});}
            var Q11;
            {var subQ5=makeQuery(id+"F21.boolean.opBoolean","INTERSECT",EDGE,{"derivedFrom":[makeQuery(id+"F1.opRevolve","SWEPT_FACE",FACE,{"disambiguationData":[OSD([sQuery(id+"F0.wireOp",EDGE,"E6")])]}),makeQuery(id+"F21.opExtrude","SWEPT_FACE",FACE,{"disambiguationData":[OSD([sQuery(id+"F20.wireOp",EDGE,"E73")])]})]});Q11=makeQuery(id+"F22.imprint","IMPRINT",FACE,{"disambiguationData":[TD([[makeQuery(id+"F22.imprint","IMPRINT",EDGE,{"derivedFrom":subQ5}),-1.0]])]});}
            extrude(context, id + "F23", {"entities" : qUnion([Q0, Q1, Q2, Q3, Q4, Q5, Q6, Q7, Q8, Q9, Q10, Q11]), "operationType" : NewBodyOperationType.REMOVE, "oppositeDirection" : true, "depth" : 16.5 * mm});
        }
    });
